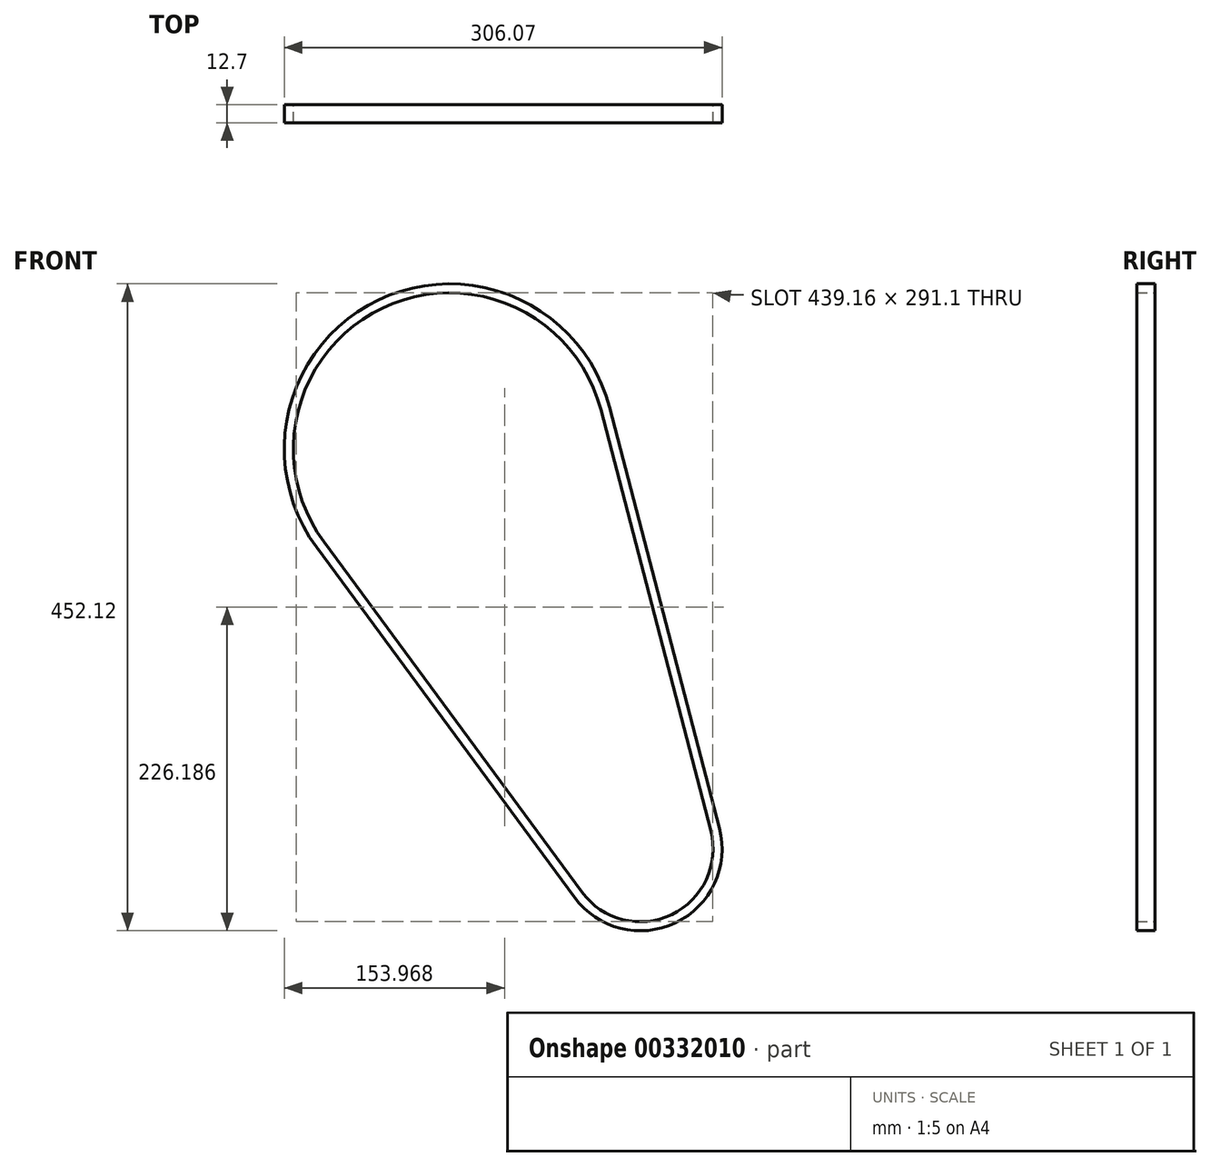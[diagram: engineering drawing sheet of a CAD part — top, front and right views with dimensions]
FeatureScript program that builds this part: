
annotation { "Feature Type Name" : "Feature", "Feature Type Description" : "" }
export const myFeature = defineFeature(function(context is Context, id is Id, definition is map)
    precondition{}
    {
        {
            var Q0;
            Q0=qCreatedBy(makeId("Front.planeOp"),FACE);
            var sketch = newSketch(context, id + "F0", { "sketchPlane" : qUnion([Q0])});
            skLineSegment(sketch, "E0", {"start": v(0, 0) * mm, "end": v(0, -279.4) * mm, "construction": true});
            skLineSegment(sketch, "E1", {"start": v(0, -279.4) * mm, "end": v(133.35, -279.4) * mm, "construction": true});
            skArc(sketch, "E2", {"start": v(105.68, 27.6) * mm, "mid": v(-47.04, 98.57) * mm, "end": v(-87.92, -64.8) * mm});
            skArc(sketch, "E3", {"start": v(92.46, -309.54) * mm, "mid": v(155.23, -325.25) * mm, "end": v(182.5, -266.56) * mm});
            skLineSegment(sketch, "E4", {"start": v(0, 0) * mm, "end": v(133.35, -279.4) * mm, "construction": true});
            skLineSegment(sketch, "E5", {"start": v(103.12, 37.4) * mm, "end": v(182.5, -266.56) * mm});
            skLineSegment(sketch, "E6.MirrorCS", {"start": v(-93.92, -56.65) * mm, "end": v(92.46, -309.54) * mm});
            skArc(sketch, "E7.0", {"start": v(111.82, 29.2) * mm, "mid": v(-49.78, 104.3) * mm, "end": v(-93.03, -68.57) * mm});
            skLineSegment(sketch, "E8.0", {"start": v(109.26, 39) * mm, "end": v(188.65, -264.96) * mm});
            skArc(sketch, "E9.0", {"start": v(87.34, -313.3) * mm, "mid": v(157.97, -330.98) * mm, "end": v(188.65, -264.96) * mm});
            skLineSegment(sketch, "E10.0", {"start": v(-99.04, -60.42) * mm, "end": v(87.34, -313.3) * mm});
            skSolve(sketch);
        }
        {
            var Q0;
            Q0=qSketchRegion(id+"F0",true);
            extrude(context, id + "F1", {"entities" : qUnion([Q0]), "endBound" : BoundingType.SYMMETRIC, "depth" : 12.7 * mm});
        }
    });
